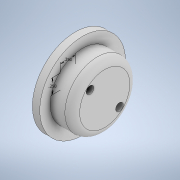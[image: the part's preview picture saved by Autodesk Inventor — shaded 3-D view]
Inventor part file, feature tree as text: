
AUTODESK INVENTOR PART (.ipt)
format: ipt  version: 2020 (Build 240168000, 168)  size: 148,480 bytes
history: native  units: in
note: dims shown in document units (in); Inventor stores cm internally (conversion verified against a paired STEP export)
features: sketch x2, hole x2, revolve x1, pattern_circular x1, fillet x1
ambient origin geometry x8: Origin, YZ Plane, XZ Plane, XY Plane, X Axis, Y Axis, Z Axis, Center Point
bodies: Solid1 (feature_tree)
feature tree (7):
  revolve  "Revolution1"  [1 undecoded]
  sketch  "Sketch2"  dims[d2=0.375in d3=0.5512in d4=90.0deg d5=0.25in d6=0.25in d7=0.213in d8=0.25in d9=0.375in d10=0.25in d11=0.5635in d12=0.25in d13=0.0in d14=0.13in d15=0.25in d16=0.119in d17=0.25in d18=0.5635in d19=0.5in d20=0.8108in d21=0.7874in d22=360.0deg d24=0.125in]
  hole  "Hole1"  [1 undecoded]
  hole  "Hole2"  [1 undecoded]
  pattern_circular  "Circular Pattern1"  [2 undecoded]
  fillet  "Fillet1"  Radius=0.25in
  sketch  "Sketch1"  dims[d0=0.125in d1=0.7283in]
note: 5 required parameter values undecoded (feature->parameter linkage not recoverable at this tier; creation-order binding heuristic only, values carry confidence <= 0.55)